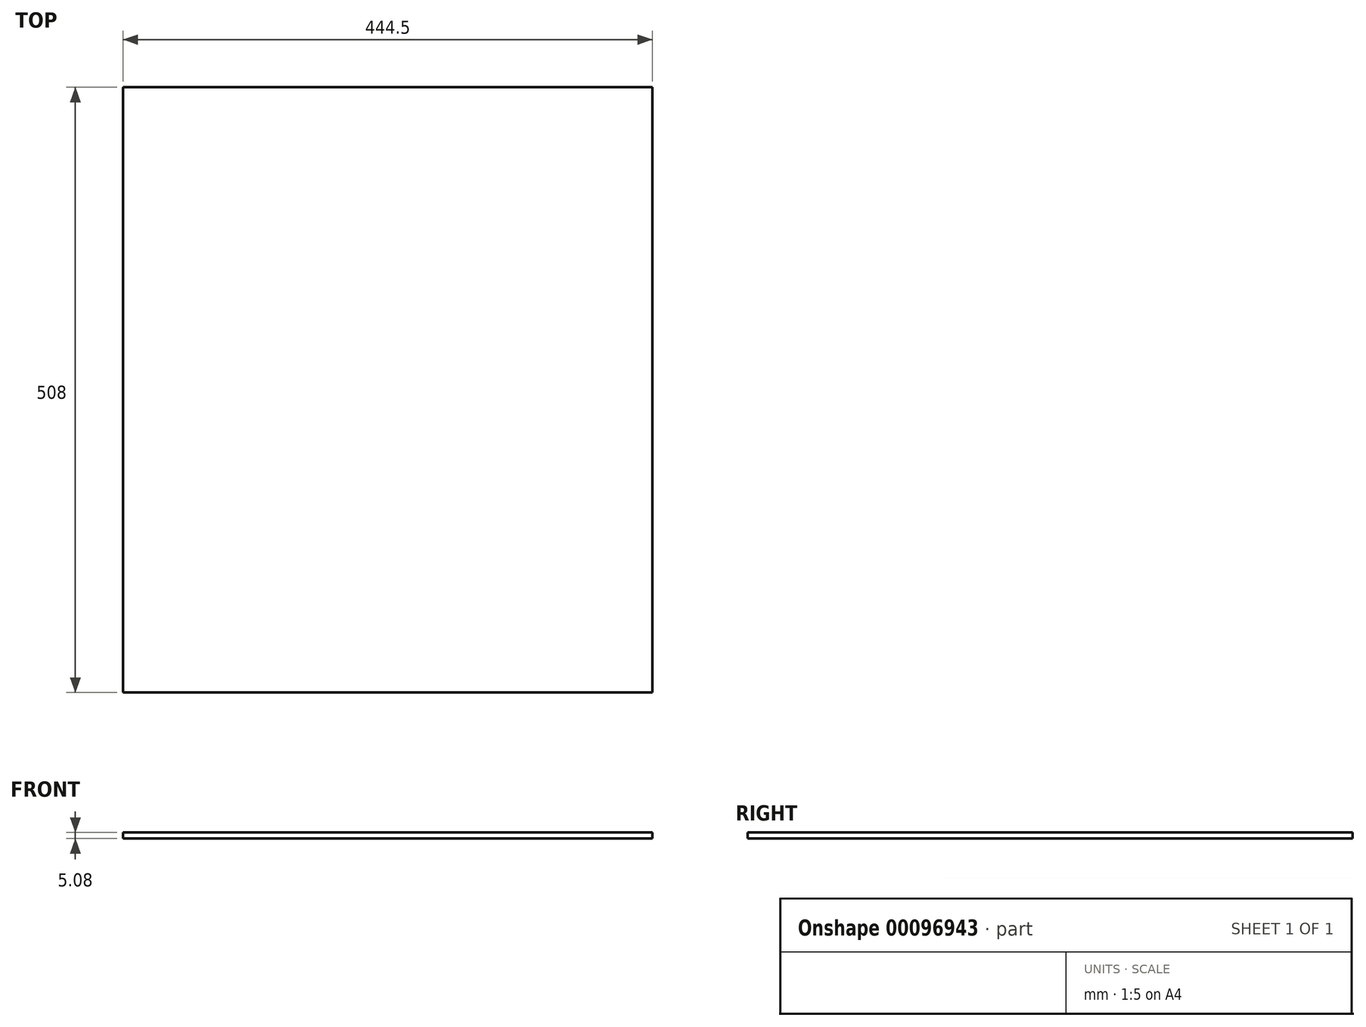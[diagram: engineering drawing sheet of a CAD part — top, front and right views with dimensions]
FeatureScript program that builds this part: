
annotation { "Feature Type Name" : "Feature", "Feature Type Description" : "" }
export const myFeature = defineFeature(function(context is Context, id is Id, definition is map)
    precondition{}
    {
        {
            var Q0;
            Q0=qCreatedBy(makeId("Top.planeOp"),FACE);
            var sketch = newSketch(context, id + "F0", { "sketchPlane" : qUnion([Q0])});
            skLineSegment(sketch, "E0.bottom", {"start": v(222.25, -254) * mm, "end": v(-222.25, -254) * mm});
            skLineSegment(sketch, "E0.top", {"start": v(222.25, 254) * mm, "end": v(-222.25, 254) * mm});
            skLineSegment(sketch, "E0.left", {"start": v(222.25, -254) * mm, "end": v(222.25, 254) * mm});
            skLineSegment(sketch, "E0.right", {"start": v(-222.25, -254) * mm, "end": v(-222.25, 254) * mm});
            skPoint(sketch, "E0.middle", {"position": v(0, 0) * mm});
            skSolve(sketch);
        }
        {
            var Q0;
            Q0=makeQuery(id+"F0.imprint","IMPRINT",FACE,{"disambiguationData":[TD([[makeQuery(id+"F0.imprint","IMPRINT",EDGE,{"derivedFrom":sQuery(id+"F0.wireOp",EDGE,"E0.bottom")}),-1.0]])]});
            extrude(context, id + "F1", {"entities" : qUnion([Q0]), "depth" : 5.08 * mm});
        }
    });
